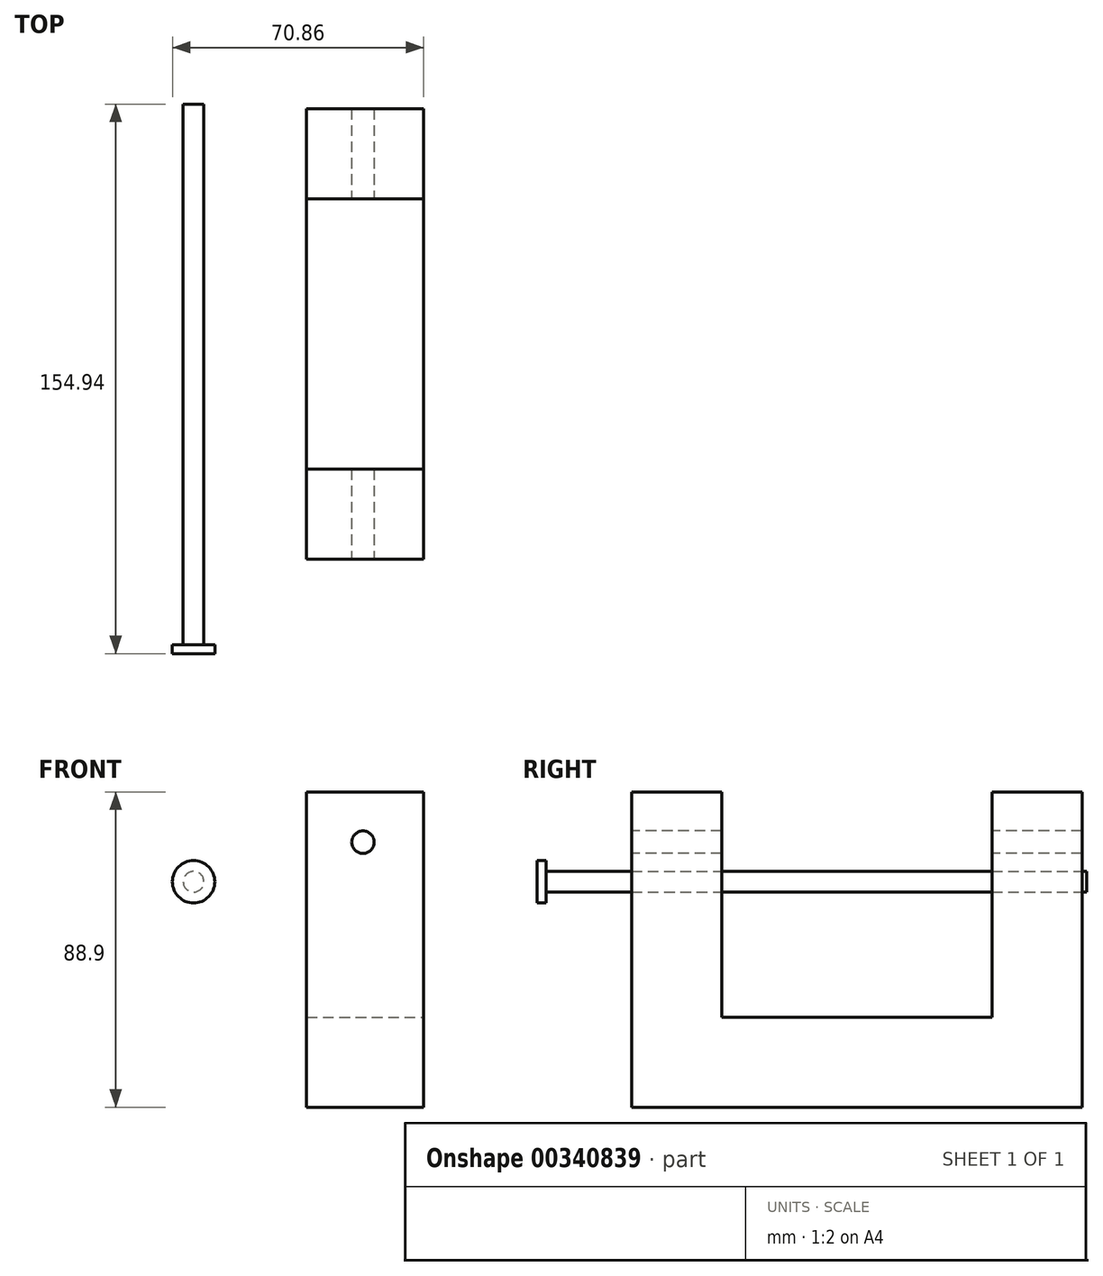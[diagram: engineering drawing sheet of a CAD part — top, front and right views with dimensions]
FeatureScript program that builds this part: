
annotation { "Feature Type Name" : "Feature", "Feature Type Description" : "" }
export const myFeature = defineFeature(function(context is Context, id is Id, definition is map)
    precondition{}
    {
        {
            var Q0;
            Q0=qCreatedBy(makeId("Right.planeOp"),FACE);
            var sketch = newSketch(context, id + "F0", { "sketchPlane" : qUnion([Q0])});
            skLineSegment(sketch, "E0.bottom", {"start": v(-52.18, -0.3) * mm, "end": v(74.82, -0.3) * mm});
            skLineSegment(sketch, "E0.top", {"start": v(-52.18, -25.7) * mm, "end": v(74.82, -25.7) * mm});
            skLineSegment(sketch, "E0.left", {"start": v(-52.18, -0.3) * mm, "end": v(-52.18, -25.7) * mm});
            skLineSegment(sketch, "E0.right", {"start": v(74.82, -0.3) * mm, "end": v(74.82, -25.7) * mm});
            skLineSegment(sketch, "E1.bottom", {"start": v(-52.18, -0.3) * mm, "end": v(-26.78, -0.3) * mm});
            skLineSegment(sketch, "E1.top", {"start": v(-52.18, 63.2) * mm, "end": v(-26.78, 63.2) * mm});
            skLineSegment(sketch, "E1.left", {"start": v(-52.18, -0.3) * mm, "end": v(-52.18, 63.2) * mm});
            skLineSegment(sketch, "E1.right", {"start": v(-26.78, -0.3) * mm, "end": v(-26.78, 63.2) * mm});
            skLineSegment(sketch, "E2.bottom", {"start": v(74.82, -0.3) * mm, "end": v(49.42, -0.3) * mm});
            skLineSegment(sketch, "E2.top", {"start": v(74.82, 63.2) * mm, "end": v(49.42, 63.2) * mm});
            skLineSegment(sketch, "E2.left", {"start": v(74.82, -0.3) * mm, "end": v(74.82, 63.2) * mm});
            skLineSegment(sketch, "E2.right", {"start": v(49.42, -0.3) * mm, "end": v(49.42, 63.2) * mm});
            skSolve(sketch);
        }
        {
            var Q0;
            Q0 = qSketchRegion(id + "F0", true);
            extrude(context, id + "F1", {"entities" : qUnion([Q0]), "oppositeDirection" : true, "depth" : 33.02 * mm});
        }
        {
            var Q0;
            Q0=makeQuery(id+"F1.opExtrude","SWEPT_FACE",FACE,{"disambiguationData":[OSD([sQuery(id+"F0.wireOp",EDGE,"E0.left"),sQuery(id+"F0.wireOp",EDGE,"E1.left")])]});
            var sketch = newSketch(context, id + "F2", { "sketchPlane" : qUnion([Q0])});
            skPoint(sketch, "E3", {"position": v(-17.14, 49) * mm});
            skSolve(sketch);
        }
        {
            var Q0;
            Q0=sQuery(id+"F2.wireOp",VERTEX,"E3");
            var Q1;
            Q1=makeQuery(id+"F1.opExtrude","SWEPT_BODY",BODY,{"disambiguationData":[OSD([sQuery(id+"F0.wireOp",EDGE,"E0.bottom"),sQuery(id+"F0.wireOp",EDGE,"E0.top"),sQuery(id+"F0.wireOp",EDGE,"E0.left"),sQuery(id+"F0.wireOp",EDGE,"E0.right"),sQuery(id+"F0.wireOp",EDGE,"E1.top"),sQuery(id+"F0.wireOp",EDGE,"E1.left"),sQuery(id+"F0.wireOp",EDGE,"E1.right"),sQuery(id+"F0.wireOp",EDGE,"E2.top"),sQuery(id+"F0.wireOp",EDGE,"E2.left"),sQuery(id+"F0.wireOp",EDGE,"E2.right")])]});
            hole(context, id + "F3", {"style" : HoleStyle.SIMPLE, "endStyle" : HoleEndStyle.THROUGH, "holeDiameter" : 6.35 * mm, "tappedDepth" : 12.7 * mm, "tapClearance" : 3, "locations" : qUnion([Q0]), "scope" : qUnion([Q1])});
        }
        {
            var Q0;
            Q0=qCreatedBy(makeId("Front.planeOp"),FACE);
            var sketch = newSketch(context, id + "F4", { "sketchPlane" : qUnion([Q0])});
            skCircle(sketch, "E4", {"center": v(-64.9, 37.84) * mm, "radius": 2.92 * mm});
            skSolve(sketch);
        }
        {
            var Q0;
            Q0=makeQuery(id+"F4.imprint","IMPRINT",FACE,{"disambiguationData":[TD([[makeQuery(id+"F4.imprint","IMPRINT",EDGE,{"derivedFrom":sQuery(id+"F4.wireOp",EDGE,"E4")}),1.0]])]});
            extrude(context, id + "F5", {"entities" : qUnion([Q0]), "depth" : 76.2 * mm, "hasSecondDirection" : true, "secondDirectionOppositeDirection" : true, "secondDirectionDepth" : 76.2 * mm});
        }
        {
            var Q0;
            Q0=makeQuery(id+"F5.opExtrude","CAP_FACE",FACE,{"disambiguationData":[OSD([sQuery(id+"F4.wireOp",EDGE,"E4")])],"isStart":false});
            var sketch = newSketch(context, id + "F6", { "sketchPlane" : qUnion([Q0])});
            skCircle(sketch, "E5", {"center": v(-64.9, 37.84) * mm, "radius": 5.97 * mm});
            skSolve(sketch);
        }
        {
            var Q0;
            Q0=makeQuery(id+"F6.imprint","IMPRINT",FACE,{"disambiguationData":[TD([[makeQuery(id+"F6.imprint","IMPRINT",EDGE,{"derivedFrom":sQuery(id+"F6.wireOp",EDGE,"E5")}),1.0]])]});
            var Q1;
            Q1=makeQuery(id+"F6.imprint","IMPRINT",FACE,{"disambiguationData":[TD([[makeQuery(id+"F6.imprint","IMPRINT",EDGE,{"derivedFrom":makeQuery(id+"F5.opExtrude","CAP_EDGE",EDGE,{"disambiguationData":[OSD([sQuery(id+"F4.wireOp",EDGE,"E4")])],"isStart":false})}),1.0]])]});
            extrude(context, id + "F7", {"entities" : qUnion([Q0, Q1]), "operationType" : NewBodyOperationType.ADD, "depth" : 2.54 * mm});
        }
    });
